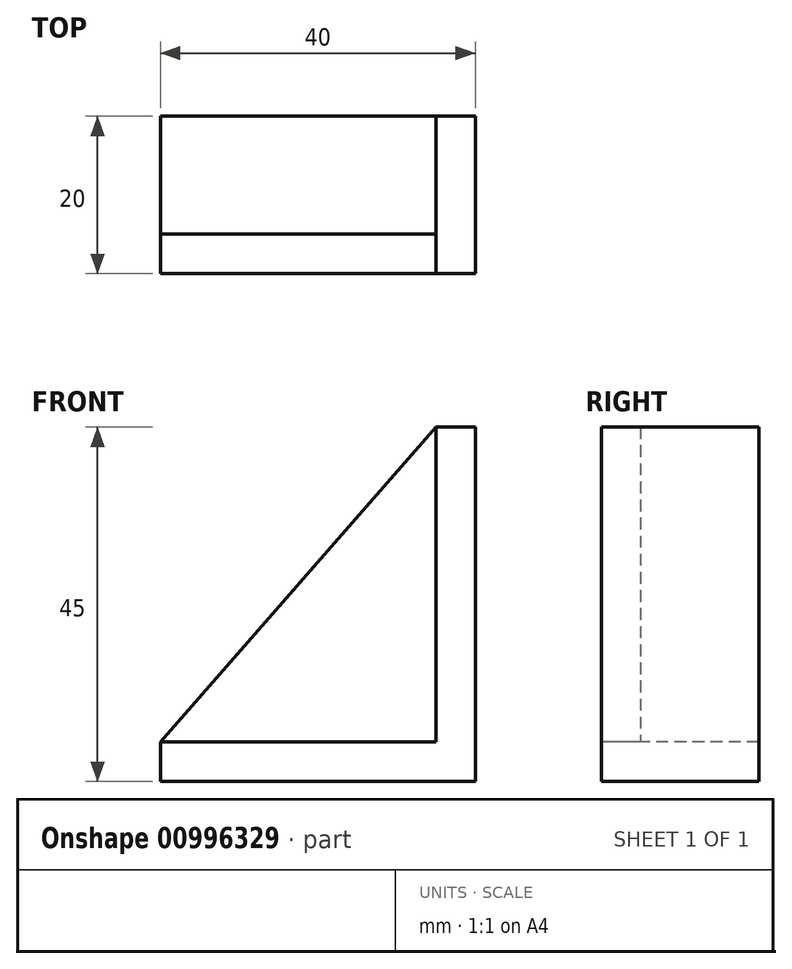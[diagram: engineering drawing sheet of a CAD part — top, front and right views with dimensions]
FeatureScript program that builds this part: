
annotation { "Feature Type Name" : "Feature", "Feature Type Description" : "" }
export const myFeature = defineFeature(function(context is Context, id is Id, definition is map)
    precondition{}
    {
        {
            var Q0;
            Q0=qCreatedBy(makeId("Top.planeOp"),FACE);
            var sketch = newSketch(context, id + "F0", { "sketchPlane" : qUnion([Q0])});
            skLineSegment(sketch, "E0.bottom", {"start": v(-20, 10) * mm, "end": v(20, 10) * mm});
            skLineSegment(sketch, "E0.top", {"start": v(-20, -10) * mm, "end": v(20, -10) * mm});
            skLineSegment(sketch, "E0.left", {"start": v(-20, 10) * mm, "end": v(-20, -10) * mm});
            skLineSegment(sketch, "E0.right", {"start": v(20, 10) * mm, "end": v(20, -10) * mm});
            skPoint(sketch, "E0.middle", {"position": v(0, 0) * mm});
            skSolve(sketch);
        }
        {
            var Q0;
            Q0 = qSketchRegion(id + "F0", true);
            extrude(context, id + "F1", {"entities" : qUnion([Q0]), "depth" : 5 * mm, "offsetDistance" : 25 * mm});
        }
        {
            var Q0;
            Q0=makeQuery(id+"F1.opExtrude","CAP_FACE",FACE,{"disambiguationData":[OSD([sQuery(id+"F0.wireOp",EDGE,"E0.bottom"),sQuery(id+"F0.wireOp",EDGE,"E0.top"),sQuery(id+"F0.wireOp",EDGE,"E0.left"),sQuery(id+"F0.wireOp",EDGE,"E0.right")])],"isStart":false});
            var sketch = newSketch(context, id + "F2", { "sketchPlane" : qUnion([Q0])});
            skLineSegment(sketch, "E1.bottom", {"start": v(20, 10) * mm, "end": v(15, 10) * mm});
            skLineSegment(sketch, "E1.top", {"start": v(20, -10) * mm, "end": v(15, -10) * mm});
            skLineSegment(sketch, "E1.left", {"start": v(20, 10) * mm, "end": v(20, -10) * mm});
            skLineSegment(sketch, "E1.right", {"start": v(15, 10) * mm, "end": v(15, -10) * mm});
            skSolve(sketch);
        }
        {
            var Q0;
            Q0 = qSketchRegion(id + "F2", true);
            extrude(context, id + "F3", {"entities" : qUnion([Q0]), "operationType" : NewBodyOperationType.ADD, "depth" : 40 * mm, "offsetDistance" : 25 * mm});
        }
        {
            var Q0;
            Q0=makeQuery(id+"F3.boolean.opBoolean","MERGE",FACE,{"derivedFrom":[makeQuery(id+"F1.opExtrude","SWEPT_FACE",FACE,{"disambiguationData":[OSD([sQuery(id+"F0.wireOp",EDGE,"E0.top")])]}),makeQuery(id+"F3.opExtrude","SWEPT_FACE",FACE,{"disambiguationData":[OSD([sQuery(id+"F2.wireOp",EDGE,"E1.top")])]})]});
            var sketch = newSketch(context, id + "F4", { "sketchPlane" : qUnion([Q0])});
            skLineSegment(sketch, "E2", {"start": v(15, 45) * mm, "end": v(-20, 5) * mm});
            skSolve(sketch);
        }
        {
            var Q0;
            Q0=makeQuery(id+"F4.imprint","IMPRINT",FACE,{"disambiguationData":[TD([[makeQuery(id+"F4.imprint","IMPRINT",EDGE,{"derivedFrom":sQuery(id+"F4.wireOp",EDGE,"E2")}),1.0]])]});
            extrude(context, id + "F5", {"entities" : qUnion([Q0]), "oppositeDirection" : true, "depth" : 5 * mm, "offsetDistance" : 25 * mm});
        }
    });
